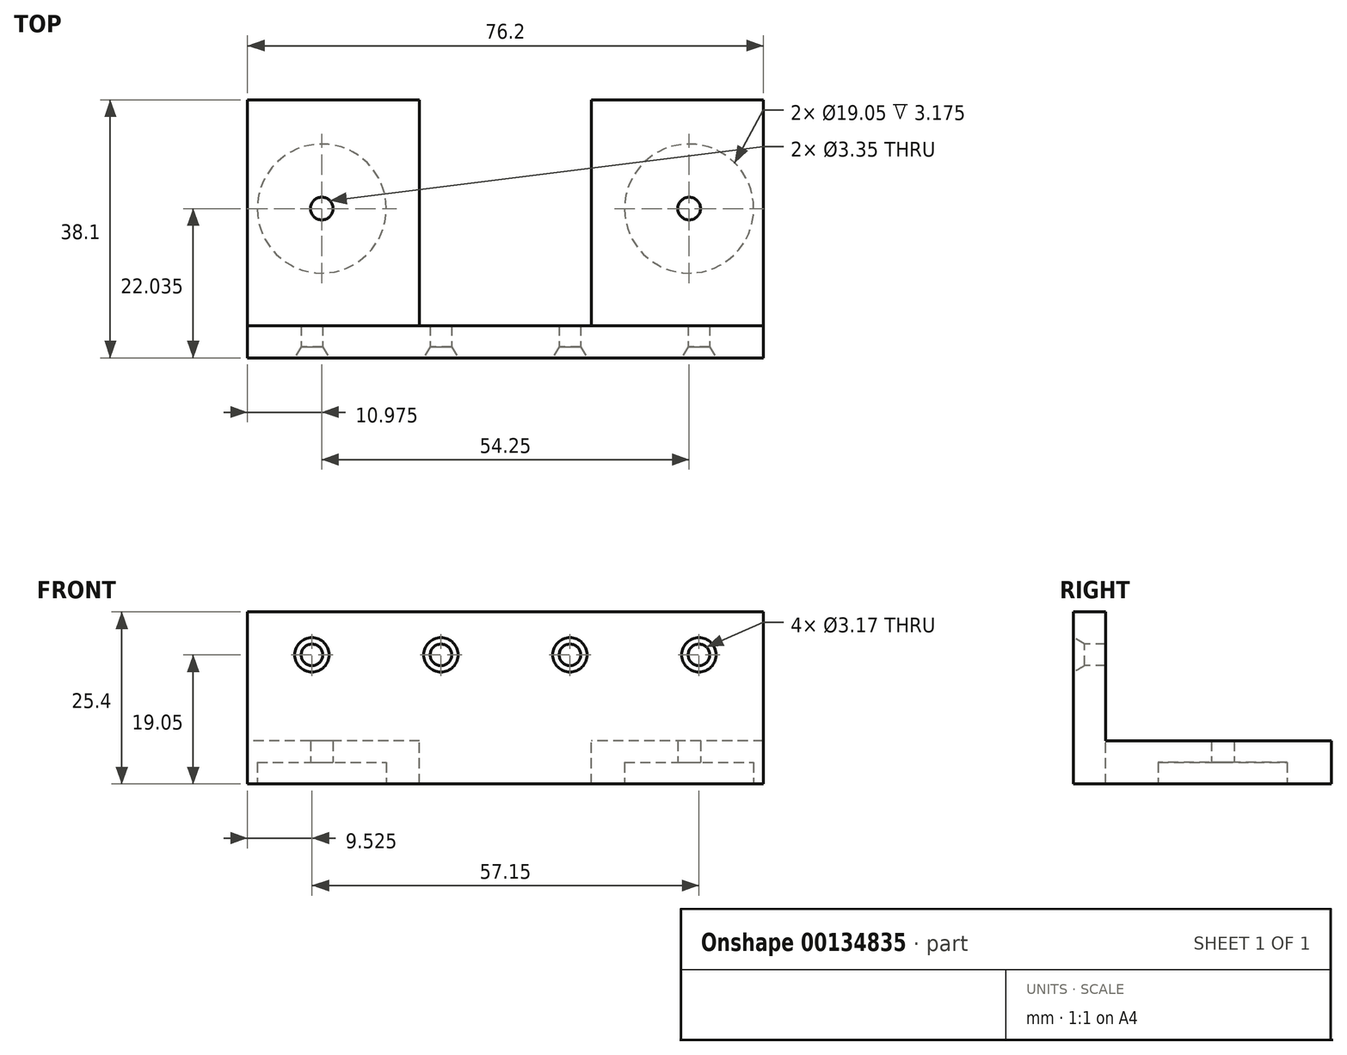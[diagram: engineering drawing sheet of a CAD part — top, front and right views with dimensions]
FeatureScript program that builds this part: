
annotation { "Feature Type Name" : "Feature", "Feature Type Description" : "" }
export const myFeature = defineFeature(function(context is Context, id is Id, definition is map)
    precondition{}
    {
        {
            var Q0;
            Q0=qCreatedBy(makeId("Right.planeOp"),FACE);
            var sketch = newSketch(context, id + "F0", { "sketchPlane" : qUnion([Q0])});
            skLineSegment(sketch, "E0", {"start": v(0, 0) * mm, "end": v(0, 25.4) * mm});
            skLineSegment(sketch, "E1", {"start": v(0, 25.4) * mm, "end": v(4.76, 25.4) * mm});
            skLineSegment(sketch, "E2", {"start": v(4.76, 25.4) * mm, "end": v(4.76, 6.35) * mm});
            skLineSegment(sketch, "E3", {"start": v(4.76, 6.35) * mm, "end": v(38.1, 6.35) * mm});
            skLineSegment(sketch, "E4", {"start": v(38.1, 6.35) * mm, "end": v(38.1, 0) * mm});
            skLineSegment(sketch, "E5", {"start": v(38.1, 0) * mm, "end": v(0, 0) * mm});
            skSolve(sketch);
        }
        {
            var Q0;
            Q0 = qSketchRegion(id + "F0", true);
            extrude(context, id + "F1", {"entities" : qUnion([Q0]), "depth" : 76.2 * mm});
        }
        {
            var Q0;
            Q0=makeQuery(id+"F1.opExtrude","SWEPT_FACE",FACE,{"disambiguationData":[OSD([sQuery(id+"F0.wireOp",EDGE,"E3")])]});
            var sketch = newSketch(context, id + "F2", { "sketchPlane" : qUnion([Q0])});
            skLineSegment(sketch, "E6.bottom", {"start": v(50.8, 4.76) * mm, "end": v(25.4, 4.76) * mm});
            skLineSegment(sketch, "E6.top", {"start": v(50.8, 38.1) * mm, "end": v(25.4, 38.1) * mm});
            skLineSegment(sketch, "E6.left", {"start": v(50.8, 4.76) * mm, "end": v(50.8, 38.1) * mm});
            skLineSegment(sketch, "E6.right", {"start": v(25.4, 4.76) * mm, "end": v(25.4, 38.1) * mm});
            skSolve(sketch);
        }
        {
            var Q0;
            Q0 = qSketchRegion(id + "F2", true);
            extrude(context, id + "F3", {"entities" : qUnion([Q0]), "operationType" : NewBodyOperationType.REMOVE, "oppositeDirection" : true, "depth" : 25.4 * mm});
        }
        {
            var Q0;
            Q0=makeQuery(id+"F1.opExtrude","SWEPT_FACE",FACE,{"disambiguationData":[OSD([sQuery(id+"F0.wireOp",EDGE,"E5")])]});
            var sketch = newSketch(context, id + "F4", { "sketchPlane" : qUnion([Q0])});
            skCircle(sketch, "E7", {"center": v(65.23, -22.03) * mm, "radius": 9.53 * mm});
            skCircle(sketch, "E8", {"center": v(10.98, -22.03) * mm, "radius": 9.53 * mm});
            skLineSegment(sketch, "E9", {"start": v(38.1, -4.76) * mm, "end": v(38.1, -40.78) * mm, "construction": true});
            skSolve(sketch);
        }
        {
            var Q0;
            Q0 = qSketchRegion(id + "F4", true);
            extrude(context, id + "F5", {"entities" : qUnion([Q0]), "operationType" : NewBodyOperationType.REMOVE, "oppositeDirection" : true, "depth" : 3.17 * mm});
        }
        {
            var Q0;
            Q0=makeQuery(id+"F1.opExtrude","SWEPT_FACE",FACE,{"disambiguationData":[OSD([sQuery(id+"F0.wireOp",EDGE,"E5")])]});
            var sketch = newSketch(context, id + "F6", { "sketchPlane" : qUnion([Q0])});
            skCircle(sketch, "E10", {"center": v(65.23, -22.03) * mm, "radius": 1.68 * mm});
            skCircle(sketch, "E11", {"center": v(10.98, -22.03) * mm, "radius": 1.68 * mm});
            skSolve(sketch);
        }
        {
            var Q0;
            Q0 = qSketchRegion(id + "F6", true);
            extrude(context, id + "F7", {"entities" : qUnion([Q0]), "operationType" : NewBodyOperationType.REMOVE, "oppositeDirection" : true, "depth" : 25.4 * mm});
        }
        {
            var Q0;
            Q0=makeQuery(id+"F1.opExtrude","SWEPT_FACE",FACE,{"disambiguationData":[OSD([sQuery(id+"F0.wireOp",EDGE,"E0")])]});
            var sketch = newSketch(context, id + "F8", { "sketchPlane" : qUnion([Q0])});
            skCircle(sketch, "E12", {"center": v(9.53, 19.05) * mm, "radius": 1.59 * mm});
            skCircle(sketch, "E13", {"center": v(28.58, 19.05) * mm, "radius": 1.59 * mm});
            skCircle(sketch, "E14", {"center": v(47.63, 19.05) * mm, "radius": 1.59 * mm});
            skCircle(sketch, "E15", {"center": v(66.68, 19.05) * mm, "radius": 1.59 * mm});
            skLineSegment(sketch, "E16", {"start": v(38.1, 25.4) * mm, "end": v(38.1, 49.14) * mm, "construction": true});
            skSolve(sketch);
        }
        {
            var Q0;
            Q0 = qSketchRegion(id + "F8", true);
            extrude(context, id + "F9", {"entities" : qUnion([Q0]), "operationType" : NewBodyOperationType.REMOVE, "oppositeDirection" : true, "depth" : 25.4 * mm});
        }
        {
            var Q0;
            Q0=makeQuery(id+"F1.opExtrude","SWEPT_FACE",FACE,{"disambiguationData":[OSD([sQuery(id+"F0.wireOp",EDGE,"E0")])]});
            var sketch = newSketch(context, id + "F10", { "sketchPlane" : qUnion([Q0])});
            skCircle(sketch, "E17", {"center": v(9.53, 19.05) * mm, "radius": 2.54 * mm});
            skCircle(sketch, "E18", {"center": v(28.58, 19.05) * mm, "radius": 2.54 * mm});
            skCircle(sketch, "E19", {"center": v(47.63, 19.05) * mm, "radius": 2.54 * mm});
            skCircle(sketch, "E20", {"center": v(66.68, 19.05) * mm, "radius": 2.54 * mm});
            skSolve(sketch);
        }
        {
            var Q0;
            Q0 = qSketchRegion(id + "F10", true);
            extrude(context, id + "F11", {"entities" : qUnion([Q0]), "operationType" : NewBodyOperationType.REMOVE, "oppositeDirection" : true, "depth" : 25.4 * mm, "hasDraft" : true, "draftAngle" : 30 * degree, "draftPullDirection" : true});
        }
    });
